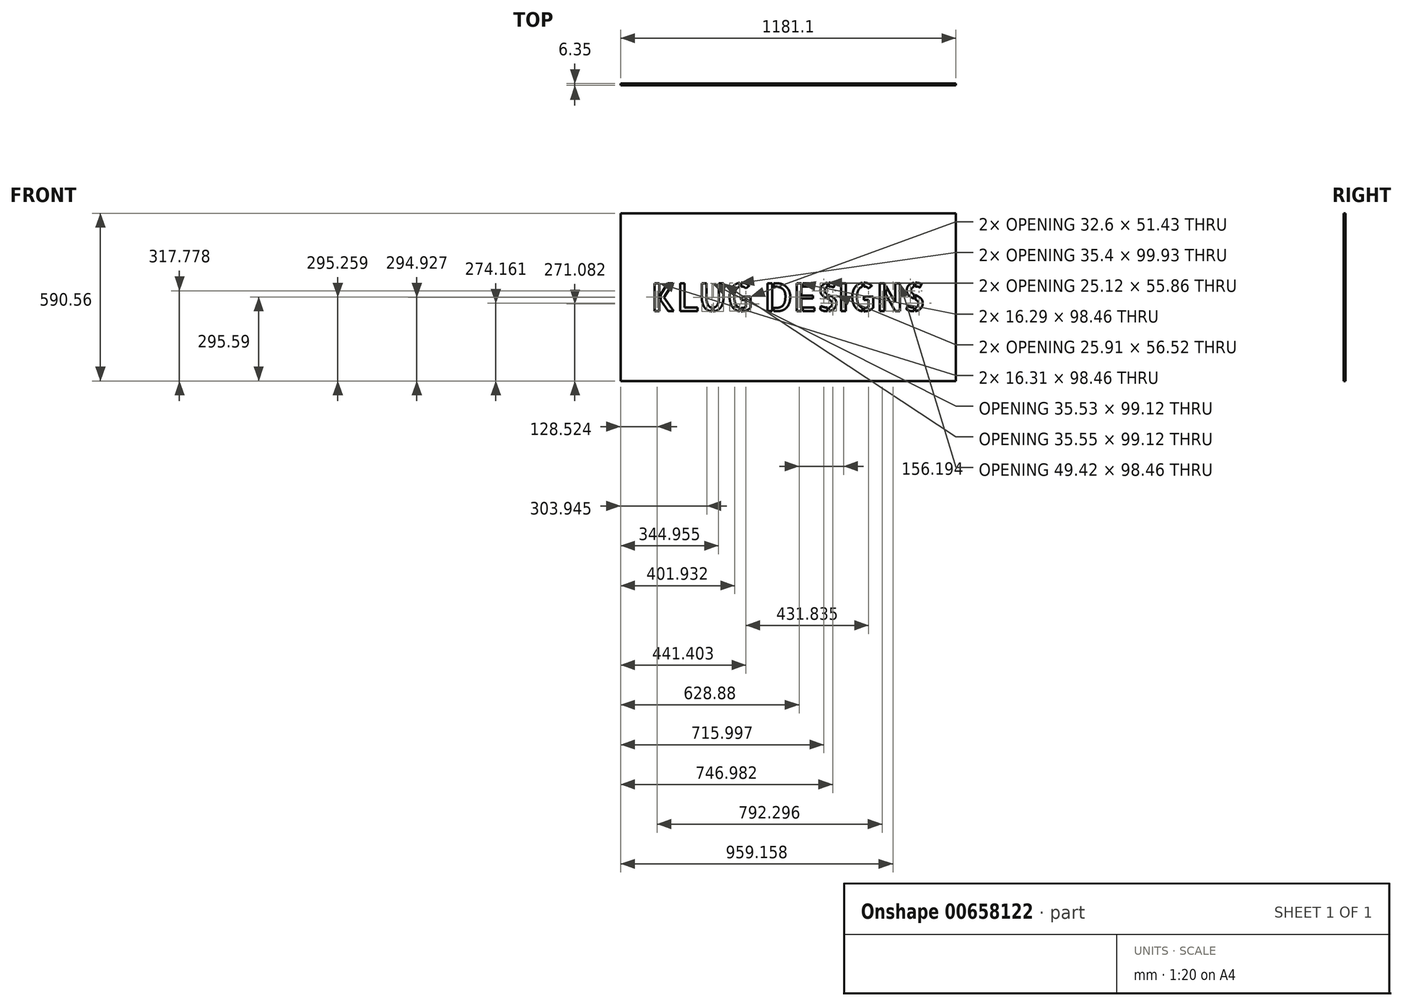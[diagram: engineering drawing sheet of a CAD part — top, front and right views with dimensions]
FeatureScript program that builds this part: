
annotation { "Feature Type Name" : "Feature", "Feature Type Description" : "" }
export const myFeature = defineFeature(function(context is Context, id is Id, definition is map)
    precondition{}
    {
        {
            var Q0;
            Q0=qCreatedBy(makeId("Front.planeOp"),FACE);
            var sketch = newSketch(context, id + "F0", { "sketchPlane" : qUnion([Q0])});
            skLineSegment(sketch, "E0.bottom", {"start": v(-590.55, -295.28) * mm, "end": v(590.55, -295.28) * mm});
            skLineSegment(sketch, "E0.top", {"start": v(-590.55, 295.28) * mm, "end": v(590.55, 295.28) * mm});
            skLineSegment(sketch, "E0.left", {"start": v(-590.55, -295.28) * mm, "end": v(-590.55, 295.28) * mm});
            skLineSegment(sketch, "E0.right", {"start": v(590.55, -295.28) * mm, "end": v(590.55, 295.28) * mm});
            skPoint(sketch, "E0.middle", {"position": v(0, 0) * mm});
            skSolve(sketch);
        }
        {
            var Q0;
            Q0=qSketchRegion(id+"F0",true);
            extrude(context, id + "F1", {"entities" : qUnion([Q0]), "depth" : 6.35 * mm, "offsetDistance" : 25.4 * mm});
        }
        {
            var Q0;
            Q0=makeQuery(id+"F1.opExtrude","CAP_FACE",FACE,{"disambiguationData":[OSD([sQuery(id+"F0.wireOp",EDGE,"E0.bottom"),sQuery(id+"F0.wireOp",EDGE,"E0.top"),sQuery(id+"F0.wireOp",EDGE,"E0.left"),sQuery(id+"F0.wireOp",EDGE,"E0.right")])],"isStart":false});
            var sketch = newSketch(context, id + "F2", { "sketchPlane" : qUnion([Q0])});
            skText(sketch, "E1", { "text": "KLUG DESIGNS", "fontName": "AllertaStencil-Regular.ttf"});
            skLineSegment(sketch, "E2", {"start": v(-482.6, 0) * mm, "end": v(482.6, 0) * mm, "construction": true});
            const initialGuessF2  = {"E1": [-0.4826, -0.04925, 1, 0, 0.0985]};
            skSetInitialGuess(sketch, initialGuessF2);
            skSolve(sketch);
        }
        {
            var Q0;
            Q0 = qSketchRegion(id + "F2", true);
            extrude(context, id + "F3", {"entities" : qUnion([Q0]), "operationType" : NewBodyOperationType.REMOVE, "endBound" : BoundingType.THROUGH_ALL, "oppositeDirection" : true, "depth" : 25.4 * mm, "offsetDistance" : 25.4 * mm});
        }
    });
